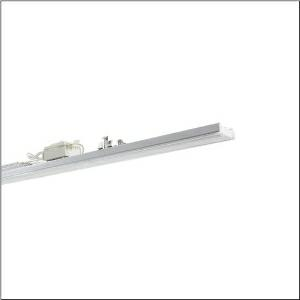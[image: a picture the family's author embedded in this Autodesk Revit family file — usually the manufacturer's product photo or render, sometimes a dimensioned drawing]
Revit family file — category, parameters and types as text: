
# Revit family: licross_11_recessed_ho_51tl12dn3dxm
name_source: partatom
category: Lighting Fixtures
units: mm (PartAtom-declared; Revit-internal decimal feet)

## family parameters
Cut with Voids When Loaded = No
Host = Face
Light Source = No
Part Type = Normal
Room Calculation Point = No
Round Connector Dimension = Use Diameter
Shared = No

## types (1)
- --- (1 x LED, 13490 lm, 76.8 W, 3000K)
    Apparent Load = 77 VA
    CIE Flux Codes = 66 91 98 100 100
    Color Rendering = 80
    Color Temperature = 3000K
    Default Elevation = 1800 mm
    Description = Licross 11 Recessed HO, luminaire insert, of sheet steel, coil coated, white, length: 1.500mm, width: 66mm, height: 67mm, LED rated luminous flux: 13.490lm, light colour: 830, SDCM (Standard Deviation of Colour Matching)MacAdam ≤ 2 SDCM (initial), control gear: DALI 2, with plug, 5-pole, with phase selection, mains connection: 220..240V, AC, 50/60Hz, rated input power: 77W, internal wiring halogen-free, primary optical cover: cover, of PMMA, light emission: direct distribution, primary light characteristic: symmetric, protection rating (complete): IP40, insulation class (complete): insulation class I (protective earthing), certification: CE, ENEC, VDE, UKCA, protection symbol: D if used in an environment without relevant dust loads with corresponding accessories, impact resistance: IK06, permissible ambient temperature for indoor applications: -25..+30°C, corresponds to IFS (International Featured Standards) requirements for safety and quality in the food industry, reducing of maximum allowable ambient temperature of 5°C with ceiling mounting, LABS conformity tested according to VDMA 24364:2018-05, The light source and the operating device comply with the requirements of the Ecodesign Regulation (EU) 2019/2020 and are replaceable in accordance with this regulation, packaging unit: 1 piece
    Height = 58 mm
    Lamp = 1 x LED
    Lamp Light Flux = 13490 lm
    Lamp Power = 76.8 W
    Lamp count = 1
    Length = 1500 mm
    Luminous efficacy = 176 lm/W
    Manufacturer = Siteco
    ModVariant = No
    Model = 51TL12DN3DXM
    Mounting Place = Ceiling
    Mounting Type = Pendant
    Number of Poles = 1
    OnlyDefault = Yes
    Power Factor = 1
    Product Name = Licross 11 Recessed HO
    Product group = luminaire insert | ceiling pendant
    ProductGroupID = 901
    Protection Class = Protection class I
    Protection Degree = IP 40
    RLX_Detail_Level = 1
    RLX_Emergency_Light_Flux = 0 lm
    RLX_Emergency_Type = 0
    RLX_Emergency_Type_DB = No
    RlxData = <blob elided: 24857 chars, md5=746567eb>
    Socket = socket
    Standby Power = 0 W
    System Light Flux = 13490 lm
    System Power = 77 W
    Type Comments = factory setting: luminous flux: 100 % | dim-lin: 254 | 522 mA
    Type Image = l_1296930.jpg
    URL = http://relux.com
    VarID = @adj_075383
    Voltage = 0 V
    Weight = 0.00 kg
    Width = 66 mm

## geometry (parser evidence)
native form markers: Blend x4, Sweep x12
no freeform markers — native parametric forms only
